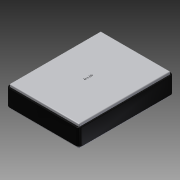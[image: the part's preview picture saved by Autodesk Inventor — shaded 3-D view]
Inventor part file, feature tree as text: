
AUTODESK INVENTOR PART (.ipt)
format: ipt  version: 2014 (Build 180170000, 170)  size: 463,360 bytes
history: native  units: mm
features: fillet x3, sketch x3, extrude x2, emboss x1
ambient origin geometry x8: Origin, YZ Plane, XZ Plane, XY Plane, X Axis, Y Axis, Z Axis, Center Point
bodies: Body1 (feature_tree)
feature tree (9):
  extrude  "Extrusion1"  Depth=111.76mm
  extrude  "Extrusion2"  Depth=2.54mm
  fillet  "Fillet1"  Radius=2.54mm
  fillet  "Fillet2"  Radius=33.02mm
  fillet  "Fillet3"  Radius=0.508mm
  emboss  "Emboss1"
  sketch  "Sketch1"  dims[d0=144.78mm d1=111.76mm]
  sketch  "Sketch2"  dims[d2=25.4mm d3=0.0mm d4=2.54mm d5=2.54mm d6=33.02mm d7=0.0mm d8=0.508mm]
  sketch  "Sketch3"  dims[d9=1.27mm d11=2.54mm d12=2.54mm d13=5.08mm d14=2.54mm d15=0.0mm]
